# Revit family: Edge_TB42_D_Top_Hung_Standard
name_source: partatom
category: Windows
revit_build: Autodesk Revit 2014 (Build: 20130308_1515(x64)
units: mm (PartAtom-declared; Revit-internal decimal feet)

## types (12) — shared parameters
Aluminium Thickness = 1 mm  [stored 0.00328084 ft]
Bead SG Gap = 13 mm
Bottom Hung = No
Casement Dimension = 42 mm  [stored 0.137795 ft]
Custom Sash Height = 554 mm  [stored 1.81759 ft]
DG Extrusion Start = 11 mm  [stored 0.0360892 ft]
DG Gasket Finish = Double Glazing Gasket Material
DG Thickness Calc = 4 mm  [stored 0.0131234 ft]
Default Sill Height = 800 mm  [stored 2.62467 ft]
Depth Bead = 28 mm  [stored 0.0918635 ft]
Description = Thermal break casement windows (42mm), Type D top hung
Frame Center Offset = 21 mm  [stored 0.0688976 ft]
Height Panel 1 = 540 mm  [stored 1.77165 ft]
Height Sash = 524 mm  [stored 1.71916 ft]
Height Sash Opening = 554 mm  [stored 1.81759 ft]
Limit Fixed Pane Height Max = 1800 mm
Limit Fixed Pane Height Min = 200 mm  [stored 0.656168 ft]
Limit Sash Height Max = 1200 mm
Limit Sash Height Min = 300 mm  [stored 0.984252 ft]
Limit Sash Width Max = 1500 mm  [stored 4.92126 ft]
Limit Sash Width Min = 300 mm  [stored 0.984252 ft]
Limit Window Height Max = 2430 mm
Limit Window Height Min = 830 mm  [stored 2.7231 ft]
Limit Window Width Max = 1546 mm  [stored 5.07218 ft]
Limit Window Width Min = 346 mm
Manufacturer = Crealco
Max System DG One Piece Thickness = 6 mm  [stored 0.019685 ft]
Max System DG Unit Thickness = 25 mm  [stored 0.082021 ft]
Model = Edge
Offset Bead SG Center Reversed = 21 mm  [stored 0.0688976 ft]
Offset Panel 3 Bead Top = 600 mm  [stored 1.9685 ft]
Offset Sash Left = 23 mm  [stored 0.0754593 ft]
Offset Sash Top = 23 mm  [stored 0.0754593 ft]
Offset Transom Top = 570 mm  [stored 1.87008 ft]
Offset Window Exterior = 21 mm  [stored 0.0688976 ft]
SG Gasket Thickness = 6 mm  [stored 0.019685 ft]
Sash Center Offset = 18 mm
Sash Overlap = 7 mm  [stored 0.0229659 ft]
Sash Spacing Inner = 8 mm  [stored 0.0262467 ft]
Top Hung = Yes
URL = http://www.crealco.co.za
Wall Closure = By host
Width Bead = 15 mm  [stored 0.0492126 ft]
Width Profile = 30 mm  [stored 0.0984252 ft]
zero-valued in all types: Window Exterior Offset

## per-type parameters (varying)
- EDGE-0609T-1000Pa: Area Pane Bottom=0.13 m²; Area Pane Top=0.23 m²; Clearvue Insulated LowE SHGC Value=0.392; Clearvue Insulated LowE U Value=2.82; Clearvue Insulated SHGC Value=0.43; Clearvue Insulated U Value=3.2; Clearvue SHGC Value=0.47; Clearvue U Value=5.17; Custom Windload=1000 mm  [stored 3.28084 ft]; Custom Window Height=890 mm  [stored 2.91995 ft]; Custom Window Width=590 mm  [stored 1.9357 ft]; Energy Advantage SHGC Value=0.421; Energy Advantage U Value=4.06; Height=890 mm  [stored 2.91995 ft]; Height Panel 3=260 mm; Intruderprufe Insulated LowE SHGC Value=0.356; Intruderprufe Insulated LowE U Value=2.77; Intruderprufe Insulated SHGC Value=0.393; Intruderprufe Insulated U Value=3.16; Intruderprufe LowE SHGC Value=0.394; Intruderprufe LowE U Value=4.07; Intruderprufe SHGC Value=0.436; Intruderprufe U Value=5.08; Length Transom=530 mm  [stored 1.73885 ft]; Max Pane Area=0.23 m²; Width=590 mm  [stored 1.9357 ft]; Width Panel 1=530 mm  [stored 1.73885 ft]; Width Panel 3=530 mm  [stored 1.73885 ft]; Width Sash=514 mm; Width Sash Opening=544 mm  [stored 1.78478 ft]; Windload Design=1000 mm  [stored 3.28084 ft]
- EDGE-0909T-1000Pa: Area Pane Bottom=0.21 m²; Area Pane Top=0.37 m²; Clearvue Insulated LowE SHGC Value=0.431; Clearvue Insulated LowE U Value=2.7; Clearvue Insulated SHGC Value=0.473; Clearvue Insulated U Value=3.14; Clearvue SHGC Value=0.521; Clearvue U Value=5.27; Custom Windload=1000 mm  [stored 3.28084 ft]; Custom Window Height=890 mm  [stored 2.91995 ft]; Custom Window Width=890 mm  [stored 2.91995 ft]; Energy Advantage SHGC Value=0.467; Energy Advantage U Value=4.02; Height=890 mm  [stored 2.91995 ft]; Height Panel 3=260 mm; Intruderprufe Insulated LowE SHGC Value=0.391; Intruderprufe Insulated LowE U Value=2.66; Intruderprufe Insulated SHGC Value=0.433; Intruderprufe Insulated U Value=3.1; Intruderprufe LowE SHGC Value=0.436; Intruderprufe LowE U Value=4.02; Intruderprufe SHGC Value=0.485; Intruderprufe U Value=5.17; Length Transom=830 mm  [stored 2.7231 ft]; Max Pane Area=0.37 m²; Width=890 mm  [stored 2.91995 ft]; Width Panel 1=830 mm  [stored 2.7231 ft]; Width Panel 3=830 mm  [stored 2.7231 ft]; Width Sash=814 mm  [stored 2.6706 ft]; Width Sash Opening=844 mm  [stored 2.76903 ft]; Windload Design=1000 mm  [stored 3.28084 ft]
- EDGE-0612T-1000Pa: Area Pane Bottom=0.29 m²; Area Pane Top=0.23 m²; Clearvue Insulated LowE SHGC Value=0.439; Clearvue Insulated LowE U Value=2.68; Clearvue Insulated SHGC Value=0.483; Clearvue Insulated U Value=3.13; Clearvue SHGC Value=0.53; Clearvue U Value=5.3; Custom Windload=1000 mm  [stored 3.28084 ft]; Custom Window Height=1190 mm  [stored 3.9042 ft]; Custom Window Width=590 mm  [stored 1.9357 ft]; Energy Advantage SHGC Value=0.475; Energy Advantage U Value=4.02; Height=1190 mm  [stored 3.9042 ft]; Height Panel 3=560 mm; Intruderprufe Insulated LowE SHGC Value=0.4; Intruderprufe Insulated LowE U Value=2.63; Intruderprufe Insulated SHGC Value=0.442; Intruderprufe Insulated U Value=3.09; Intruderprufe LowE SHGC Value=0.444; Intruderprufe LowE U Value=4.01; Intruderprufe SHGC Value=0.494; Intruderprufe U Value=5.2; Length Transom=530 mm  [stored 1.73885 ft]; Max Pane Area=0.29 m²; Width=590 mm  [stored 1.9357 ft]; Width Panel 1=530 mm  [stored 1.73885 ft]; Width Panel 3=530 mm  [stored 1.73885 ft]; Width Sash=514 mm; Width Sash Opening=544 mm  [stored 1.78478 ft]; Windload Design=1000 mm  [stored 3.28084 ft]
- EDGE-0912T-1000Pa: Area Pane Bottom=0.45 m²; Area Pane Top=0.37 m²; Clearvue Insulated LowE SHGC Value=0.477; Clearvue Insulated LowE U Value=2.56; Clearvue Insulated SHGC Value=0.524; Clearvue Insulated U Value=3.07; Clearvue SHGC Value=0.581; Clearvue U Value=5.39; Custom Windload=1000 mm  [stored 3.28084 ft]; Custom Window Height=1190 mm  [stored 3.9042 ft]; Custom Window Width=890 mm  [stored 2.91995 ft]; Energy Advantage SHGC Value=0.52; Energy Advantage U Value=3.97; Height=1190 mm  [stored 3.9042 ft]; Height Panel 3=560 mm; Intruderprufe Insulated LowE SHGC Value=0.435; Intruderprufe Insulated LowE U Value=2.52; Intruderprufe Insulated SHGC Value=0.481; Intruderprufe Insulated U Value=3.02; Intruderprufe LowE SHGC Value=0.485; Intruderprufe LowE U Value=3.96; Intruderprufe SHGC Value=0.542; Intruderprufe U Value=5.29; Length Transom=830 mm  [stored 2.7231 ft]; Max Pane Area=0.45 m²; Width=890 mm  [stored 2.91995 ft]; Width Panel 1=830 mm  [stored 2.7231 ft]; Width Panel 3=830 mm  [stored 2.7231 ft]; Width Sash=814 mm  [stored 2.6706 ft]; Width Sash Opening=844 mm  [stored 2.76903 ft]; Windload Design=1000 mm  [stored 3.28084 ft]
- EDGE-0609T-1500Pa: Area Pane Bottom=0.13 m²; Area Pane Top=0.23 m²; Clearvue Insulated LowE SHGC Value=0.392; Clearvue Insulated LowE U Value=2.82; Clearvue Insulated SHGC Value=0.43; Clearvue Insulated U Value=3.2; Clearvue SHGC Value=0.47; Clearvue U Value=5.17; Custom Windload=1500 mm  [stored 4.92126 ft]; Custom Window Height=890 mm  [stored 2.91995 ft]; Custom Window Width=590 mm  [stored 1.9357 ft]; Energy Advantage SHGC Value=0.421; Energy Advantage U Value=4.06; Height=890 mm  [stored 2.91995 ft]; Height Panel 3=260 mm; Intruderprufe Insulated LowE SHGC Value=0.356; Intruderprufe Insulated LowE U Value=2.77; Intruderprufe Insulated SHGC Value=0.393; Intruderprufe Insulated U Value=3.16; Intruderprufe LowE SHGC Value=0.394; Intruderprufe LowE U Value=4.07; Intruderprufe SHGC Value=0.436; Intruderprufe U Value=5.08; Length Transom=530 mm  [stored 1.73885 ft]; Max Pane Area=0.23 m²; Width=590 mm  [stored 1.9357 ft]; Width Panel 1=530 mm  [stored 1.73885 ft]; Width Panel 3=530 mm  [stored 1.73885 ft]; Width Sash=514 mm; Width Sash Opening=544 mm  [stored 1.78478 ft]; Windload Design=1500 mm  [stored 4.92126 ft]
- EDGE-0609T-2000Pa: Area Pane Bottom=0.13 m²; Area Pane Top=0.23 m²; Clearvue Insulated LowE SHGC Value=0.392; Clearvue Insulated LowE U Value=2.82; Clearvue Insulated SHGC Value=0.43; Clearvue Insulated U Value=3.2; Clearvue SHGC Value=0.47; Clearvue U Value=5.17; Custom Windload=2000 mm; Custom Window Height=890 mm  [stored 2.91995 ft]; Custom Window Width=590 mm  [stored 1.9357 ft]; Energy Advantage SHGC Value=0.421; Energy Advantage U Value=4.06; Height=890 mm  [stored 2.91995 ft]; Height Panel 3=260 mm; Intruderprufe Insulated LowE SHGC Value=0.356; Intruderprufe Insulated LowE U Value=2.77; Intruderprufe Insulated SHGC Value=0.393; Intruderprufe Insulated U Value=3.16; Intruderprufe LowE SHGC Value=0.394; Intruderprufe LowE U Value=4.07; Intruderprufe SHGC Value=0.436; Intruderprufe U Value=5.08; Length Transom=530 mm  [stored 1.73885 ft]; Max Pane Area=0.23 m²; Width=590 mm  [stored 1.9357 ft]; Width Panel 1=530 mm  [stored 1.73885 ft]; Width Panel 3=530 mm  [stored 1.73885 ft]; Width Sash=514 mm; Width Sash Opening=544 mm  [stored 1.78478 ft]; Windload Design=2000 mm
- EDGE-0909T-1500Pa: Area Pane Bottom=0.21 m²; Area Pane Top=0.37 m²; Clearvue Insulated LowE SHGC Value=0.431; Clearvue Insulated LowE U Value=2.7; Clearvue Insulated SHGC Value=0.473; Clearvue Insulated U Value=3.14; Clearvue SHGC Value=0.521; Clearvue U Value=5.27; Custom Windload=1500 mm  [stored 4.92126 ft]; Custom Window Height=890 mm  [stored 2.91995 ft]; Custom Window Width=890 mm  [stored 2.91995 ft]; Energy Advantage SHGC Value=0.467; Energy Advantage U Value=4.02; Height=890 mm  [stored 2.91995 ft]; Height Panel 3=260 mm; Intruderprufe Insulated LowE SHGC Value=0.391; Intruderprufe Insulated LowE U Value=2.66; Intruderprufe Insulated SHGC Value=0.433; Intruderprufe Insulated U Value=3.1; Intruderprufe LowE SHGC Value=0.436; Intruderprufe LowE U Value=4.02; Intruderprufe SHGC Value=0.485; Intruderprufe U Value=5.17; Length Transom=830 mm  [stored 2.7231 ft]; Max Pane Area=0.37 m²; Width=890 mm  [stored 2.91995 ft]; Width Panel 1=830 mm  [stored 2.7231 ft]; Width Panel 3=830 mm  [stored 2.7231 ft]; Width Sash=814 mm  [stored 2.6706 ft]; Width Sash Opening=844 mm  [stored 2.76903 ft]; Windload Design=1500 mm  [stored 4.92126 ft]
- EDGE-0909T-2000Pa: Area Pane Bottom=0.21 m²; Area Pane Top=0.37 m²; Clearvue Insulated LowE SHGC Value=0.431; Clearvue Insulated LowE U Value=2.7; Clearvue Insulated SHGC Value=0.473; Clearvue Insulated U Value=3.14; Clearvue SHGC Value=0.521; Clearvue U Value=5.27; Custom Windload=2000 mm; Custom Window Height=890 mm  [stored 2.91995 ft]; Custom Window Width=890 mm  [stored 2.91995 ft]; Energy Advantage SHGC Value=0.467; Energy Advantage U Value=4.02; Height=890 mm  [stored 2.91995 ft]; Height Panel 3=260 mm; Intruderprufe Insulated LowE SHGC Value=0.391; Intruderprufe Insulated LowE U Value=2.66; Intruderprufe Insulated SHGC Value=0.433; Intruderprufe Insulated U Value=3.1; Intruderprufe LowE SHGC Value=0.436; Intruderprufe LowE U Value=4.02; Intruderprufe SHGC Value=0.485; Intruderprufe U Value=5.17; Length Transom=830 mm  [stored 2.7231 ft]; Max Pane Area=0.37 m²; Width=890 mm  [stored 2.91995 ft]; Width Panel 1=830 mm  [stored 2.7231 ft]; Width Panel 3=830 mm  [stored 2.7231 ft]; Width Sash=814 mm  [stored 2.6706 ft]; Width Sash Opening=844 mm  [stored 2.76903 ft]; Windload Design=2000 mm
- EDGE-0612T-1500Pa: Area Pane Bottom=0.29 m²; Area Pane Top=0.23 m²; Clearvue Insulated LowE SHGC Value=0.439; Clearvue Insulated LowE U Value=2.68; Clearvue Insulated SHGC Value=0.483; Clearvue Insulated U Value=3.13; Clearvue SHGC Value=0.53; Clearvue U Value=5.3; Custom Windload=1500 mm  [stored 4.92126 ft]; Custom Window Height=1190 mm  [stored 3.9042 ft]; Custom Window Width=590 mm  [stored 1.9357 ft]; Energy Advantage SHGC Value=0.475; Energy Advantage U Value=4.02; Height=1190 mm  [stored 3.9042 ft]; Height Panel 3=560 mm; Intruderprufe Insulated LowE SHGC Value=0.4; Intruderprufe Insulated LowE U Value=2.63; Intruderprufe Insulated SHGC Value=0.442; Intruderprufe Insulated U Value=3.09; Intruderprufe LowE SHGC Value=0.444; Intruderprufe LowE U Value=4.01; Intruderprufe SHGC Value=0.494; Intruderprufe U Value=5.2; Length Transom=530 mm  [stored 1.73885 ft]; Max Pane Area=0.29 m²; Width=590 mm  [stored 1.9357 ft]; Width Panel 1=530 mm  [stored 1.73885 ft]; Width Panel 3=530 mm  [stored 1.73885 ft]; Width Sash=514 mm; Width Sash Opening=544 mm  [stored 1.78478 ft]; Windload Design=1500 mm  [stored 4.92126 ft]
- EDGE-0612T-2000Pa: Area Pane Bottom=0.29 m²; Area Pane Top=0.23 m²; Clearvue Insulated LowE SHGC Value=0.439; Clearvue Insulated LowE U Value=2.68; Clearvue Insulated SHGC Value=0.483; Clearvue Insulated U Value=3.13; Clearvue SHGC Value=0.53; Clearvue U Value=5.3; Custom Windload=2000 mm; Custom Window Height=1190 mm  [stored 3.9042 ft]; Custom Window Width=590 mm  [stored 1.9357 ft]; Energy Advantage SHGC Value=0.475; Energy Advantage U Value=4.02; Height=1190 mm  [stored 3.9042 ft]; Height Panel 3=560 mm; Intruderprufe Insulated LowE SHGC Value=0.4; Intruderprufe Insulated LowE U Value=2.63; Intruderprufe Insulated SHGC Value=0.442; Intruderprufe Insulated U Value=3.09; Intruderprufe LowE SHGC Value=0.444; Intruderprufe LowE U Value=4.01; Intruderprufe SHGC Value=0.494; Intruderprufe U Value=5.2; Length Transom=530 mm  [stored 1.73885 ft]; Max Pane Area=0.29 m²; Width=590 mm  [stored 1.9357 ft]; Width Panel 1=530 mm  [stored 1.73885 ft]; Width Panel 3=530 mm  [stored 1.73885 ft]; Width Sash=514 mm; Width Sash Opening=544 mm  [stored 1.78478 ft]; Windload Design=2000 mm
- EDGE-0912T-1500Pa: Area Pane Bottom=0.45 m²; Area Pane Top=0.37 m²; Clearvue Insulated LowE SHGC Value=0.477; Clearvue Insulated LowE U Value=2.56; Clearvue Insulated SHGC Value=0.524; Clearvue Insulated U Value=3.07; Clearvue SHGC Value=0.581; Clearvue U Value=5.39; Custom Windload=1500 mm  [stored 4.92126 ft]; Custom Window Height=1190 mm  [stored 3.9042 ft]; Custom Window Width=890 mm  [stored 2.91995 ft]; Energy Advantage SHGC Value=0.52; Energy Advantage U Value=3.97; Height=1190 mm  [stored 3.9042 ft]; Height Panel 3=560 mm; Intruderprufe Insulated LowE SHGC Value=0.435; Intruderprufe Insulated LowE U Value=2.52; Intruderprufe Insulated SHGC Value=0.481; Intruderprufe Insulated U Value=3.02; Intruderprufe LowE SHGC Value=0.485; Intruderprufe LowE U Value=3.96; Intruderprufe SHGC Value=0.542; Intruderprufe U Value=5.29; Length Transom=830 mm  [stored 2.7231 ft]; Max Pane Area=0.45 m²; Width=890 mm  [stored 2.91995 ft]; Width Panel 1=830 mm  [stored 2.7231 ft]; Width Panel 3=830 mm  [stored 2.7231 ft]; Width Sash=814 mm  [stored 2.6706 ft]; Width Sash Opening=844 mm  [stored 2.76903 ft]; Windload Design=1500 mm  [stored 4.92126 ft]
- EDGE-0912T-2000Pa: Area Pane Bottom=0.45 m²; Area Pane Top=0.37 m²; Clearvue Insulated LowE SHGC Value=0.477; Clearvue Insulated LowE U Value=2.56; Clearvue Insulated SHGC Value=0.524; Clearvue Insulated U Value=3.07; Clearvue SHGC Value=0.581; Clearvue U Value=5.39; Custom Windload=2000 mm; Custom Window Height=1190 mm  [stored 3.9042 ft]; Custom Window Width=890 mm  [stored 2.91995 ft]; Energy Advantage SHGC Value=0.52; Energy Advantage U Value=3.97; Height=1190 mm  [stored 3.9042 ft]; Height Panel 3=560 mm; Intruderprufe Insulated LowE SHGC Value=0.435; Intruderprufe Insulated LowE U Value=2.52; Intruderprufe Insulated SHGC Value=0.481; Intruderprufe Insulated U Value=3.02; Intruderprufe LowE SHGC Value=0.485; Intruderprufe LowE U Value=3.96; Intruderprufe SHGC Value=0.542; Intruderprufe U Value=5.29; Length Transom=830 mm  [stored 2.7231 ft]; Max Pane Area=0.45 m²; Width=890 mm  [stored 2.91995 ft]; Width Panel 1=830 mm  [stored 2.7231 ft]; Width Panel 3=830 mm  [stored 2.7231 ft]; Width Sash=814 mm  [stored 2.6706 ft]; Width Sash Opening=844 mm  [stored 2.76903 ft]; Windload Design=2000 mm

note: [stored X ft] marks values corroborated as IEEE doubles in the binary element streams (Revit-internal decimal feet)

## geometry (parser evidence)
native form markers: Blend x4, Extrusion x1, Sweep x20
no freeform markers — native parametric forms only
